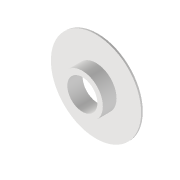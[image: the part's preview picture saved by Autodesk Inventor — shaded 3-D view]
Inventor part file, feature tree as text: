
AUTODESK INVENTOR PART (.ipt)
format: ipt  version: 2022 (Build 260153000, 153)  size: 94,720 bytes
history: native  units: mm
features: extrude x2, sketch x2, projected_geometry x1
ambient origin geometry x8: Origin, YZ Plane, XZ Plane, XY Plane, X Axis, Y Axis, Z Axis, Center Point
bodies: Volumenkörper1 (feature_tree)
feature tree (5):
  extrude  "Extrusion1"  Depth=11.0mm
  extrude  "Extrusion2"  Depth=5.0mm
  sketch  "Skizze1"  dims[d0=33.0mm d1=11.0mm]
  sketch  "Skizze2"  dims[d2=0.6mm d3=0.0mm d4=15.0mm d5=5.0mm d6=0.0mm]
  projected_geometry  "Projizierte Kontur1"
